# Revit family: Gira_0211 09-0188 005
name_source: partatom
category: Elektroinstallationen
revit_build: Autodesk Revit 2018 (Build: 20170223_1515(x64)
units: mm (PartAtom-declared; Revit-internal decimal feet)

## family parameters
Basisbauteil = Fläche
Beim Laden mit Abzugskörper schneiden = Nein
Bemaßung runder Anschluss = Durchmesser verwenden
Beschriftungsausrichtung beibehalten = Ja
Gemeinsam genutzt = Nein
Raumberechnungspunkt = Nein
Teiletyp = Normal

## types (1)
- Gira SCHUKO-Steckdose, Design E2 Schwarz matt
    Abschließbar = Nein
    Anschlussart = Steckklemme
    Antibakterielle Behandlung = Nein
    Anzahl der Einheiten = 1
    Anzahl der Module (bei Modulbauweise) = 1
    Anzahl der Steckdosen schaltbar = 0
    Aufdruck/Kennzeichnung = ohne Aufdruck
    Ausführung = Schuko
    Ausführung der Oberfläche = matt
    Auswurfmechanismus = Nein
    BIM = https://media.live.bim.site SCHUKO-Steckdose, Design E2 Schwarz matt.rfa
    BIMSITE_PRODUCT_ID = 80c3f9127070beb1fbb330b1e29ae4eb1c32b2f7
    Befestigungsart = Krallen-/Schraubbefestigung
    Beschreibung = Abdeckrahmen Gira E2 Schwarz matt 1fach + SCHUKO-Steckdose 16 A 250 V~  Schwarz matt  Merkmale:  Bruchsicher.  Hinweise :  Auch für Kanalinstallationen geeignet.  Abdeckrahmen (1- bis 5fach) in Verbindung mit Dichtungsset auch für die Montage wassergeschützt Unterputz IP44 geeignet.
    Breite [mm] Number = 80.8
    Datenblatt = https://media.live.bim.site
    Datenblatt 1 = https://media.live.bim.site
    Datenblatt 2 = https://media.live.bim.site
    Datenblatt 3 = https://media.live.bim.site
    Datenblatt 4 = https://media.live.bim.site
    Datenblatt 5 = https://media.live.bim.site
    Farbe = schwarz
    Fehlerstromschutz = Nein
    Frequenz [Hz] = [50:50]
    Für "erschwerte Bedingungen" (nach VDE) = Nein
    GTIN = 4010337036739 + 4010337037491
    Geeignet für Schutzart (IP) = IP20
    HAN = 0211 09 + 0188 005
    Halogenfrei = Ja
    HeinzeBIM = https://www.heinze.de
    Hersteller = Gira
    Höhe [mm] Number = 80.8
    Isolierter Einbau = Nein
    Ist System = Nein
    Ist Zubehör = Nein
    Kosten = 0 $
    Material = Schwarz matt
    Mit Durchschleiffunktion = Nein
    Mit Ein-/Ausschalter = Nein
    Mit Feinsicherung = Nein
    Mit Funktionsbeleuchtung = Ja
    Mit Klappdeckel = Nein
    Mit Orientierungsbeleuchtung = Nein
    Mit Signallampe = Nein
    Mit eingebauter USB-Spannungsversorgung = Nein
    Mit erhöhtem Berührungsschutz = Nein
    Montageart = Unterputz
    Nennspannung [Volt] = 250
    Nennstrom = 16 A
    Oberfläche = sonstige
    Produktseite = https://media.live.bim.site
    Schutzkontakt = Ja
    Schutzleiterkontakt rund = Nein
    Sonderstromversorgung = ohne Sonderstromversorgung
    Textfeld/Beschriftungsfläche = Nein
    Tiefe [mm] Number = 9.3
    Transparent = Nein
    Typname = Gira SCHUKO-Steckdose, Design E2 Schwarz matt
    URL = https://www.gira.de
    Verdrehter Zentraleinsatz = Nein
    Vorgabe-Ansicht = 1219 mm
    Werkstoff = Kunststoff
    Werkstoffgüte = Thermoplast
    Überspannungsschutz = Nein

## geometry (parser evidence)
native form markers: Sweep x3
no freeform markers — native parametric forms only
